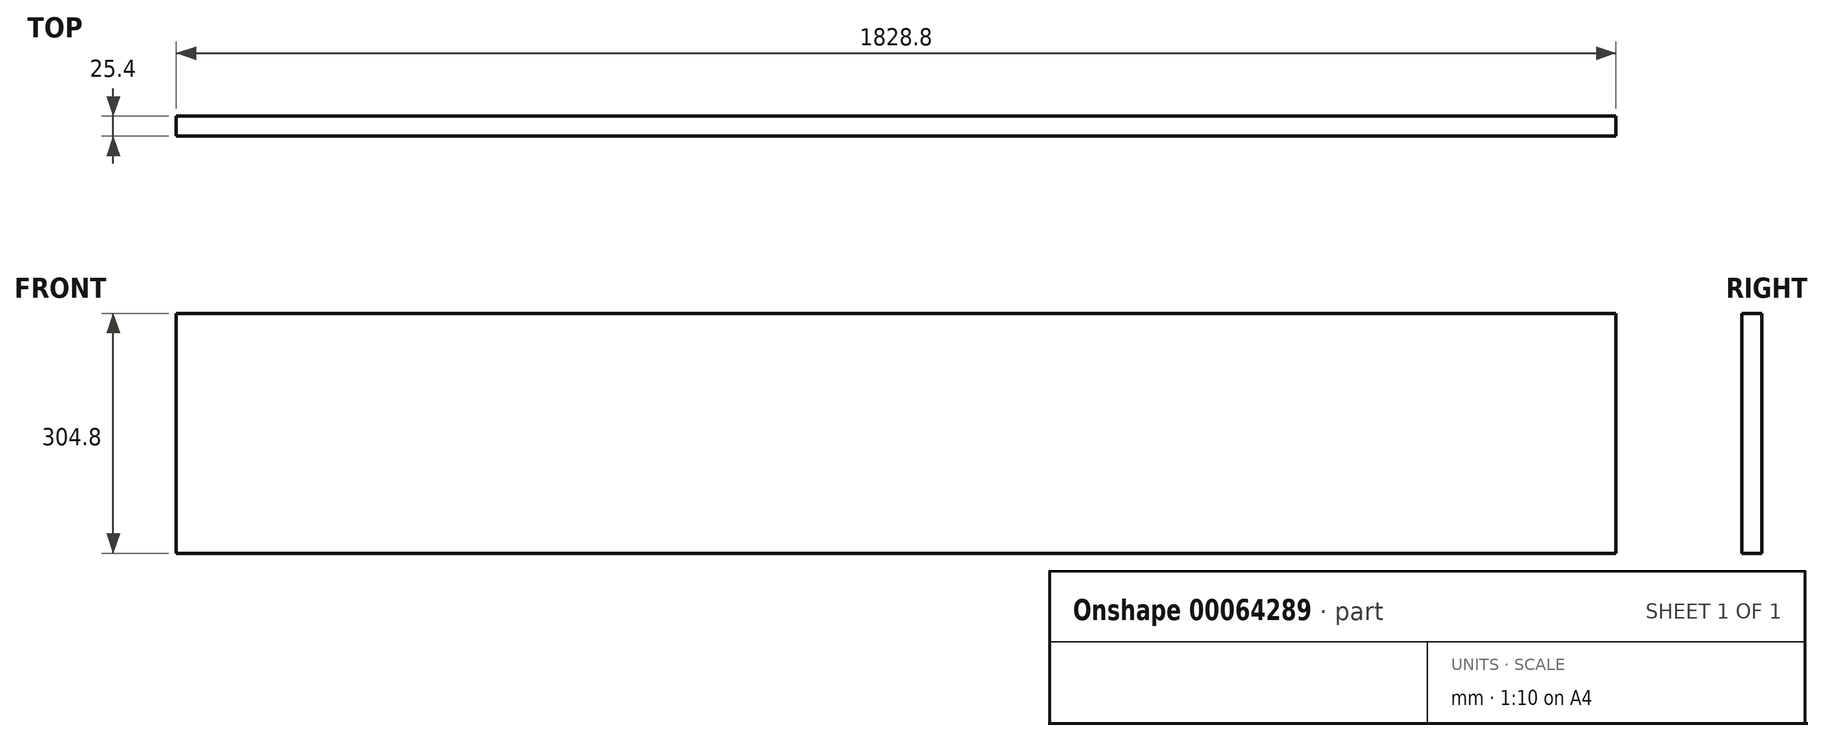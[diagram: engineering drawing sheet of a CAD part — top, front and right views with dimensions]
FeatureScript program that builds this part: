
annotation { "Feature Type Name" : "Feature", "Feature Type Description" : "" }
export const myFeature = defineFeature(function(context is Context, id is Id, definition is map)
    precondition{}
    {
        {
            var Q0;
            Q0=qCreatedBy(makeId("Front.planeOp"),FACE);
            var sketch = newSketch(context, id + "F0", { "sketchPlane" : qUnion([Q0])});
            skLineSegment(sketch, "E0.bottom", {"start": v(-914.4, -152.4) * mm, "end": v(914.4, -152.4) * mm});
            skLineSegment(sketch, "E0.top", {"start": v(-914.4, 152.4) * mm, "end": v(914.4, 152.4) * mm});
            skLineSegment(sketch, "E0.left", {"start": v(-914.4, -152.4) * mm, "end": v(-914.4, 152.4) * mm});
            skLineSegment(sketch, "E0.right", {"start": v(914.4, -152.4) * mm, "end": v(914.4, 152.4) * mm});
            skLineSegment(sketch, "E1", {"start": v(-914.4, 0) * mm, "end": v(0, 0) * mm, "construction": true});
            skLineSegment(sketch, "E2", {"start": v(0, 152.4) * mm, "end": v(0, 0) * mm, "construction": true});
            skSolve(sketch);
        }
        {
            var Q0;
            Q0=makeQuery(id+"F0.imprint","IMPRINT",FACE,{"disambiguationData":[TD([[makeQuery(id+"F0.imprint","IMPRINT",EDGE,{"derivedFrom":sQuery(id+"F0.wireOp",EDGE,"E0.bottom")}),1.0]])]});
            extrude(context, id + "F1", {"entities" : qUnion([Q0]), "depth" : 25.4 * mm});
        }
    });
